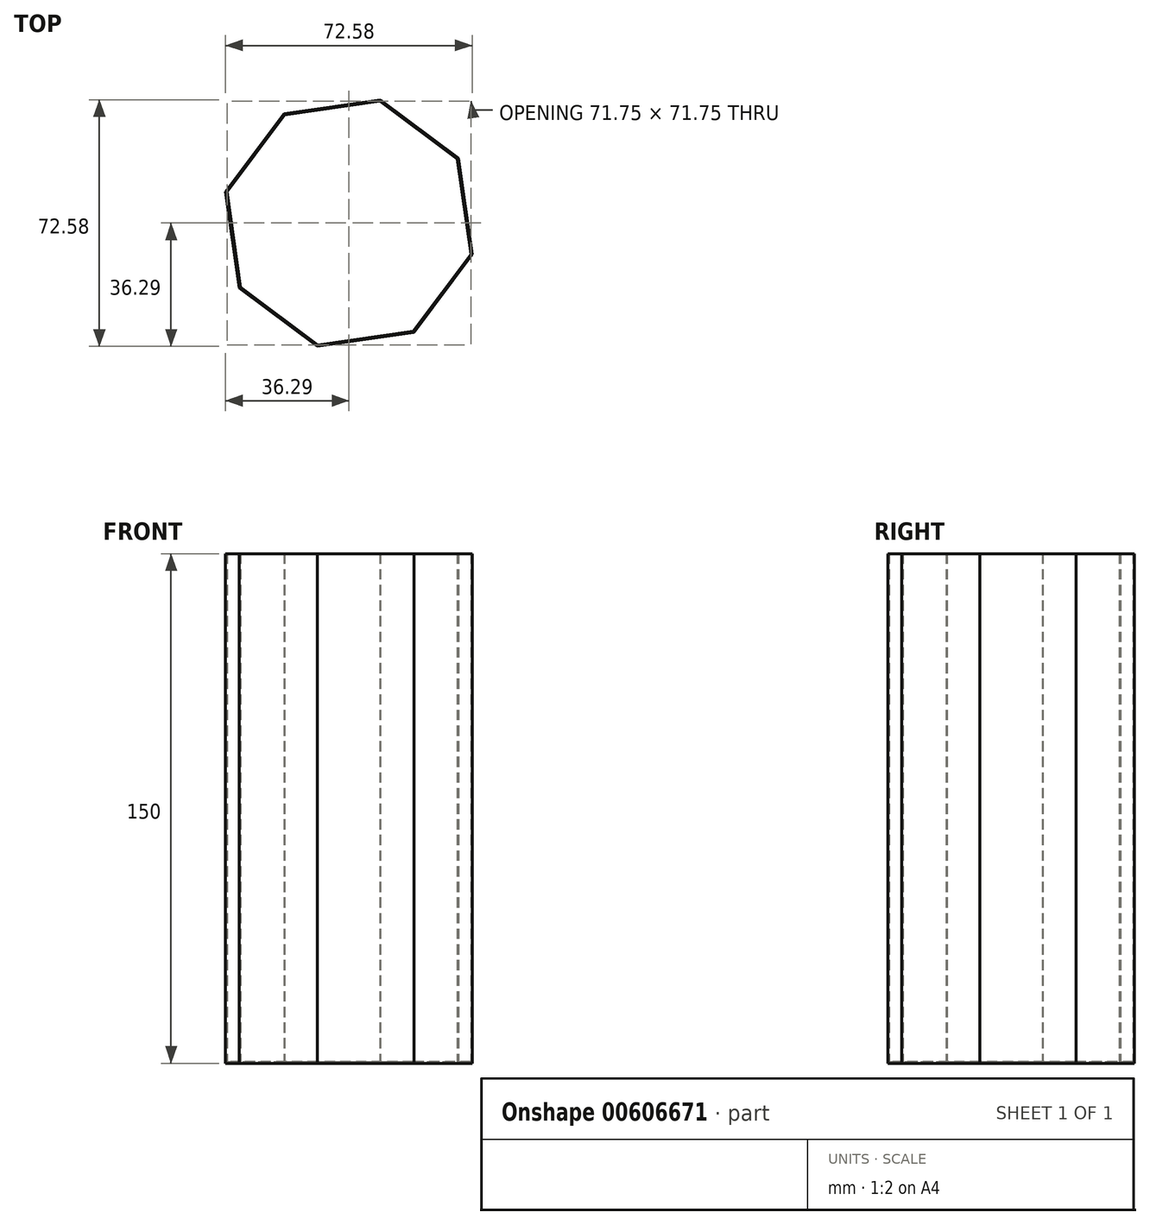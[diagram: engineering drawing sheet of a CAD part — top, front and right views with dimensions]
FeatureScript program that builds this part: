
annotation { "Feature Type Name" : "Feature", "Feature Type Description" : "" }
export const myFeature = defineFeature(function(context is Context, id is Id, definition is map)
    precondition{}
    {
        {
            var Q0;
            Q0=qCreatedBy(makeId("Top.planeOp"),FACE);
            var sketch = newSketch(context, id + "F0", { "sketchPlane" : qUnion([Q0])});
            skCircle(sketch, "E0.cCircle", {"center": v(0, 0) * mm, "radius": 34.6 * mm, "construction": true});
            skLineSegment(sketch, "E0.0", {"start": v(9.26, 36.3) * mm, "end": v(32.21, 19.11) * mm});
            skLineSegment(sketch, "E0.1", {"start": v(32.21, 19.11) * mm, "end": v(36.3, -9.26) * mm});
            skLineSegment(sketch, "E0.2", {"start": v(36.3, -9.26) * mm, "end": v(19.11, -32.21) * mm});
            skLineSegment(sketch, "E0.3", {"start": v(19.11, -32.21) * mm, "end": v(-9.26, -36.3) * mm});
            skLineSegment(sketch, "E0.4", {"start": v(-9.26, -36.3) * mm, "end": v(-32.21, -19.11) * mm});
            skLineSegment(sketch, "E0.5", {"start": v(-32.21, -19.11) * mm, "end": v(-36.3, 9.26) * mm});
            skLineSegment(sketch, "E0.6", {"start": v(-36.3, 9.26) * mm, "end": v(-19.11, 32.21) * mm});
            skLineSegment(sketch, "E0.7", {"start": v(-19.11, 32.21) * mm, "end": v(9.26, 36.3) * mm});
            skPoint(sketch, "E0.0.midPoint", {"position": v(20.74, 27.7) * mm});
            skSolve(sketch);
        }
        {
            var Q0;
            Q0=makeQuery(id+"F0.imprint","IMPRINT",FACE,{"disambiguationData":[TD([[makeQuery(id+"F0.imprint","IMPRINT",EDGE,{"derivedFrom":sQuery(id+"F0.wireOp",EDGE,"E0.0")}),-1.0]])]});
            extrude(context, id + "F1", {"entities" : qUnion([Q0]), "depth" : 150 * mm, "offsetDistance" : 25 * mm});
        }
        {
            var Q0;
            Q0=makeQuery(id+"F1.opExtrude","CAP_FACE",FACE,{"disambiguationData":[OSD([sQuery(id+"F0.wireOp",EDGE,"E0.0"),sQuery(id+"F0.wireOp",EDGE,"E0.1"),sQuery(id+"F0.wireOp",EDGE,"E0.2"),sQuery(id+"F0.wireOp",EDGE,"E0.3"),sQuery(id+"F0.wireOp",EDGE,"E0.4"),sQuery(id+"F0.wireOp",EDGE,"E0.5"),sQuery(id+"F0.wireOp",EDGE,"E0.6"),sQuery(id+"F0.wireOp",EDGE,"E0.7")])],"isStart":false});
            shell(context, id + "F2", {"entities" : qUnion([Q0]), "thickness" : 0.4 * mm});
        }
        {
            var Q0;
            Q0=makeQuery(id+"F1.opExtrude","SWEPT_BODY",BODY,{"disambiguationData":[OSD([sQuery(id+"F0.wireOp",EDGE,"E0.0"),sQuery(id+"F0.wireOp",EDGE,"E0.1"),sQuery(id+"F0.wireOp",EDGE,"E0.2"),sQuery(id+"F0.wireOp",EDGE,"E0.3"),sQuery(id+"F0.wireOp",EDGE,"E0.4"),sQuery(id+"F0.wireOp",EDGE,"E0.5"),sQuery(id+"F0.wireOp",EDGE,"E0.6"),sQuery(id+"F0.wireOp",EDGE,"E0.7")])]});
            transform(context, id + "F3", {"entities" : qUnion([Q0]), "transformType" : TransformType.TRANSLATION_3D, "dx" : 0 * mm, "dy" : 0 * mm, "dz" : 0 * mm, "makeCopy" : true});
        }
    });
